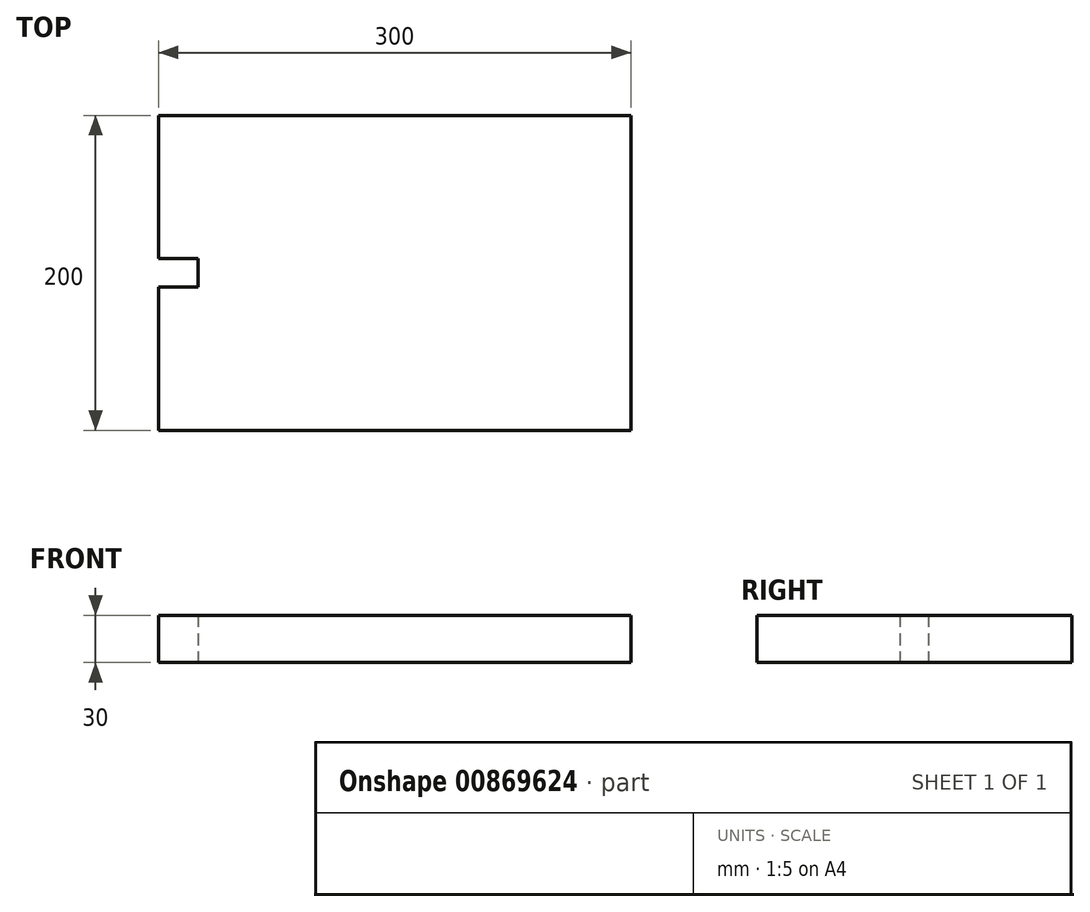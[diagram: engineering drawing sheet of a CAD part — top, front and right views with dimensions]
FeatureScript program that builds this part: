
annotation { "Feature Type Name" : "Feature", "Feature Type Description" : "" }
export const myFeature = defineFeature(function(context is Context, id is Id, definition is map)
    precondition{}
    {
        {
            var Q0;
            Q0=qCreatedBy(makeId("Top.planeOp"),FACE);
            var sketch = newSketch(context, id + "F0", { "sketchPlane" : qUnion([Q0])});
            skLineSegment(sketch, "E0.bottom", {"start": v(150, -100) * mm, "end": v(-150, -100) * mm});
            skLineSegment(sketch, "E0.top", {"start": v(150, 100) * mm, "end": v(-150, 100) * mm});
            skLineSegment(sketch, "E0.left", {"start": v(150, -100) * mm, "end": v(150, 100) * mm});
            skLineSegment(sketch, "E0.right", {"start": v(-150, -100) * mm, "end": v(-150, 100) * mm});
            skPoint(sketch, "E0.middle", {"position": v(0, 0) * mm});
            skLineSegment(sketch, "E1", {"start": v(-150, 0) * mm, "end": v(-125, 0) * mm});
            skLineSegment(sketch, "E2.bottom", {"start": v(-125, -9) * mm, "end": v(-150, -9) * mm});
            skLineSegment(sketch, "E2.top", {"start": v(-125, 9) * mm, "end": v(-150, 9) * mm});
            skLineSegment(sketch, "E2.left", {"start": v(-125, -9) * mm, "end": v(-125, 9) * mm});
            skLineSegment(sketch, "E2.right", {"start": v(-150, -9) * mm, "end": v(-150, 9) * mm});
            skPoint(sketch, "E2.middle", {"position": v(-137.5, 0) * mm});
            skSolve(sketch);
        }
        {
            var Q0;
            {var subQ1=sQuery(id+"F0.wireOp",EDGE,"E0.bottom");Q0=makeQuery(id+"F0.imprint","IMPRINT",FACE,{"disambiguationData":[TD([[makeQuery(id+"F0.imprint","IMPRINT",EDGE,{"derivedFrom":subQ1}),-1.0]])]});}
            extrude(context, id + "F1", {"entities" : qUnion([Q0]), "depth" : 30 * mm, "offsetDistance" : 25 * mm});
        }
    });
